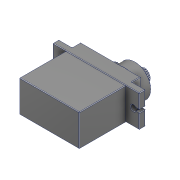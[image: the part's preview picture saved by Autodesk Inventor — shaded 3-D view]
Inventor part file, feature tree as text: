
AUTODESK INVENTOR PART (.ipt)
format: ipt  version: 2020 (Build 240168000, 168)  size: 294,912 bytes
history: mixed  units: mm
features: fillet x2, imported_body x1
ambient origin geometry x8: Origin, YZ Plane, XZ Plane, XY Plane, X Axis, Y Axis, Z Axis, Center Point
bodies: Solid1 (imported_parasolid), Solid2 (imported_parasolid)
feature tree (3):
  fillet  "Fillet1"  [1 undecoded]
  fillet  "Fillet3"  [1 undecoded]
  imported_body  NMx_Import_Brep_tag  [imported B-rep: ~32 faces, bbox_mm=[22.5, 11.8, 27.3]]
note: 2 required parameter values undecoded (feature->parameter linkage not recoverable at this tier; creation-order binding heuristic only, values carry confidence <= 0.55)
